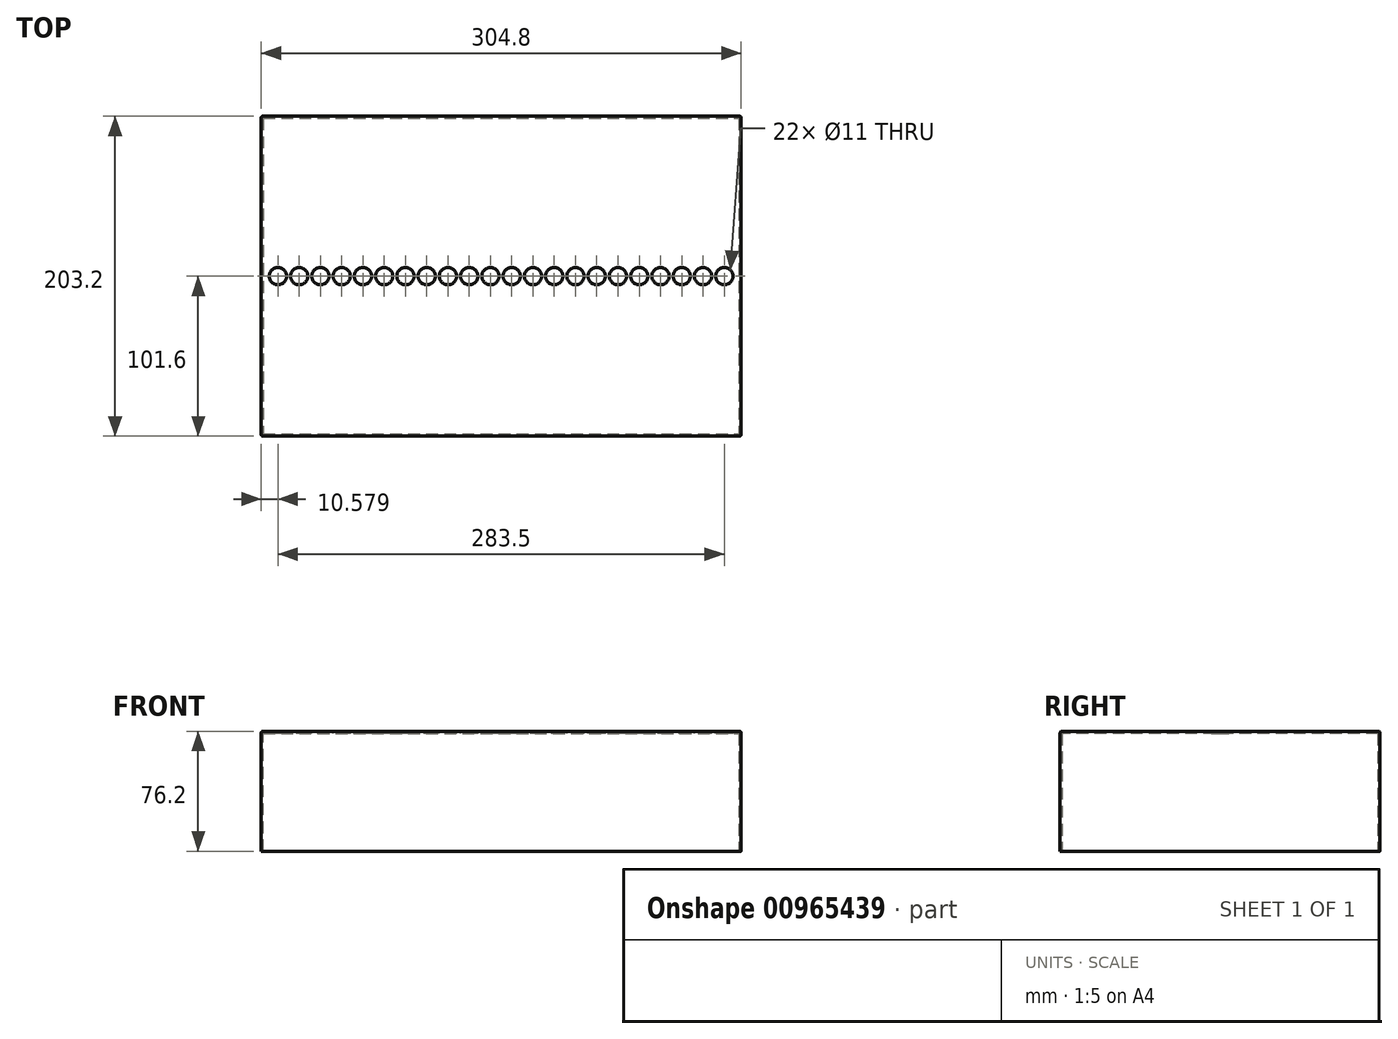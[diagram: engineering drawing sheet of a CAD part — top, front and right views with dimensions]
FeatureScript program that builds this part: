
annotation { "Feature Type Name" : "Feature", "Feature Type Description" : "" }
export const myFeature = defineFeature(function(context is Context, id is Id, definition is map)
    precondition{}
    {
        {
            var Q0;
            Q0=qCreatedBy(makeId("Top.planeOp"),FACE);
            var sketch = newSketch(context, id + "F0", { "sketchPlane" : qUnion([Q0])});
            skLineSegment(sketch, "E0.bottom", {"start": v(-152.4, 101.6) * mm, "end": v(152.4, 101.6) * mm});
            skLineSegment(sketch, "E0.top", {"start": v(-152.4, -101.6) * mm, "end": v(152.4, -101.6) * mm});
            skLineSegment(sketch, "E0.left", {"start": v(-152.4, 101.6) * mm, "end": v(-152.4, -101.6) * mm});
            skLineSegment(sketch, "E0.right", {"start": v(152.4, 101.6) * mm, "end": v(152.4, -101.6) * mm});
            skPoint(sketch, "E0.middle", {"position": v(0, 0) * mm});
            skSolve(sketch);
        }
        {
            var Q0;
            Q0 = qSketchRegion(id + "F0", true);
            extrude(context, id + "F1", {"entities" : qUnion([Q0]), "depth" : 76.2 * mm, "offsetDistance" : 25 * mm});
        }
        {
            var Q0;
            Q0=makeQuery(id+"F1.opExtrude","CAP_EDGE",EDGE,{"disambiguationData":[OSD([sQuery(id+"F0.wireOp",EDGE,"E0.top")])],"isStart":false});
            var Q1;
            Q1=makeQuery(id+"F1.opExtrude","SWEPT_EDGE",EDGE,{"disambiguationData":[OSD([sQuery(id+"F0.wireOp",EDGE,"E0.top"),sQuery(id+"F0.wireOp",EDGE,"E0.left")])]});
            var Q2;
            Q2=makeQuery(id+"F1.opExtrude","CAP_EDGE",EDGE,{"disambiguationData":[OSD([sQuery(id+"F0.wireOp",EDGE,"E0.left")])],"isStart":false});
            var Q3;
            Q3=makeQuery(id+"F1.opExtrude","CAP_EDGE",EDGE,{"disambiguationData":[OSD([sQuery(id+"F0.wireOp",EDGE,"E0.right")])],"isStart":false});
            var Q4;
            Q4=makeQuery(id+"F1.opExtrude","CAP_EDGE",EDGE,{"disambiguationData":[OSD([sQuery(id+"F0.wireOp",EDGE,"E0.bottom")])],"isStart":false});
            var Q5;
            Q5=makeQuery(id+"F1.opExtrude","SWEPT_EDGE",EDGE,{"disambiguationData":[OSD([sQuery(id+"F0.wireOp",EDGE,"E0.bottom"),sQuery(id+"F0.wireOp",EDGE,"E0.right")])]});
            var Q6;
            Q6=makeQuery(id+"F1.opExtrude","SWEPT_EDGE",EDGE,{"disambiguationData":[OSD([sQuery(id+"F0.wireOp",EDGE,"E0.top"),sQuery(id+"F0.wireOp",EDGE,"E0.right")])]});
            var Q7;
            Q7=makeQuery(id+"F1.opExtrude","SWEPT_EDGE",EDGE,{"disambiguationData":[OSD([sQuery(id+"F0.wireOp",EDGE,"E0.bottom"),sQuery(id+"F0.wireOp",EDGE,"E0.left")])]});
            fillet(context, id + "F2", {"entities" : qUnion([Q0, Q1, Q2, Q3, Q4, Q5, Q6, Q7]), "radius" : 1 * mm, "tangentPropagation" : true, "allowEdgeOverflow" : false});
        }
        {
            var Q0;
            Q0=makeQuery(id+"F1.opExtrude","CAP_FACE",FACE,{"disambiguationData":[OSD([sQuery(id+"F0.wireOp",EDGE,"E0.bottom"),sQuery(id+"F0.wireOp",EDGE,"E0.top"),sQuery(id+"F0.wireOp",EDGE,"E0.left"),sQuery(id+"F0.wireOp",EDGE,"E0.right")])],"isStart":true});
            shell(context, id + "F3", {"entities" : qUnion([Q0]), "thickness" : 1.3 * mm});
        }
        {
            var Q0;
            Q0=makeQuery(id+"F1.opExtrude","CAP_FACE",FACE,{"disambiguationData":[OSD([sQuery(id+"F0.wireOp",EDGE,"E0.bottom"),sQuery(id+"F0.wireOp",EDGE,"E0.top"),sQuery(id+"F0.wireOp",EDGE,"E0.left"),sQuery(id+"F0.wireOp",EDGE,"E0.right")])],"isStart":false});
            var sketch = newSketch(context, id + "F4", { "sketchPlane" : qUnion([Q0])});
            skLineSegment(sketch, "E1", {"start": v(-204.18, 0) * mm, "end": v(190.05, 0) * mm, "construction": true});
            skCircle(sketch, "E2", {"center": v(-141.82, 0) * mm, "radius": 5.5 * mm});
            skCircle(sketch, "E3.1.0.0", {"center": v(-128.32, 0) * mm, "radius": 5.5 * mm});
            skCircle(sketch, "E3.2.0.0", {"center": v(-114.82, 0) * mm, "radius": 5.5 * mm});
            skCircle(sketch, "E3.3.0.0", {"center": v(-101.32, 0) * mm, "radius": 5.5 * mm});
            skCircle(sketch, "E3.4.0.0", {"center": v(-87.82, 0) * mm, "radius": 5.5 * mm});
            skCircle(sketch, "E3.5.0.0", {"center": v(-74.32, 0) * mm, "radius": 5.5 * mm});
            skCircle(sketch, "E3.6.0.0", {"center": v(-60.82, 0) * mm, "radius": 5.5 * mm});
            skCircle(sketch, "E3.7.0.0", {"center": v(-47.32, 0) * mm, "radius": 5.5 * mm});
            skCircle(sketch, "E3.8.0.0", {"center": v(-33.82, 0) * mm, "radius": 5.5 * mm});
            skCircle(sketch, "E3.9.0.0", {"center": v(-20.32, 0) * mm, "radius": 5.5 * mm});
            skCircle(sketch, "E3.10.0.0", {"center": v(-6.82, 0) * mm, "radius": 5.5 * mm});
            skCircle(sketch, "E3.11.0.0", {"center": v(6.68, 0) * mm, "radius": 5.5 * mm});
            skCircle(sketch, "E3.12.0.0", {"center": v(20.18, 0) * mm, "radius": 5.5 * mm});
            skCircle(sketch, "E3.13.0.0", {"center": v(33.68, 0) * mm, "radius": 5.5 * mm});
            skCircle(sketch, "E3.14.0.0", {"center": v(47.18, 0) * mm, "radius": 5.5 * mm});
            skCircle(sketch, "E3.15.0.0", {"center": v(60.68, 0) * mm, "radius": 5.5 * mm});
            skCircle(sketch, "E3.16.0.0", {"center": v(74.18, 0) * mm, "radius": 5.5 * mm});
            skCircle(sketch, "E3.17.0.0", {"center": v(87.68, 0) * mm, "radius": 5.5 * mm});
            skCircle(sketch, "E3.18.0.0", {"center": v(101.18, 0) * mm, "radius": 5.5 * mm});
            skCircle(sketch, "E3.19.0.0", {"center": v(114.68, 0) * mm, "radius": 5.5 * mm});
            skCircle(sketch, "E3.20.0.0", {"center": v(128.18, 0) * mm, "radius": 5.5 * mm});
            skCircle(sketch, "E3.21.0.0", {"center": v(141.68, 0) * mm, "radius": 5.5 * mm});
            skLineSegment(sketch, "E3.direction1", {"start": v(-141.82, 0) * mm, "end": v(-128.32, 0) * mm, "construction": true});
            skLineSegment(sketch, "E4", {"start": v(0, 115.73) * mm, "end": v(0, -128.04) * mm, "construction": true});
            skPoint(sketch, "E4.startSnap0", {"position": v(0, 100.6) * mm});
            skSolve(sketch);
        }
        {
            var Q0;
            Q0 = qSketchRegion(id + "F4", true);
            extrude(context, id + "F5", {"entities" : qUnion([Q0]), "operationType" : NewBodyOperationType.REMOVE, "endBound" : BoundingType.THROUGH_ALL, "oppositeDirection" : true, "depth" : 25 * mm, "offsetDistance" : 25 * mm});
        }
    });
